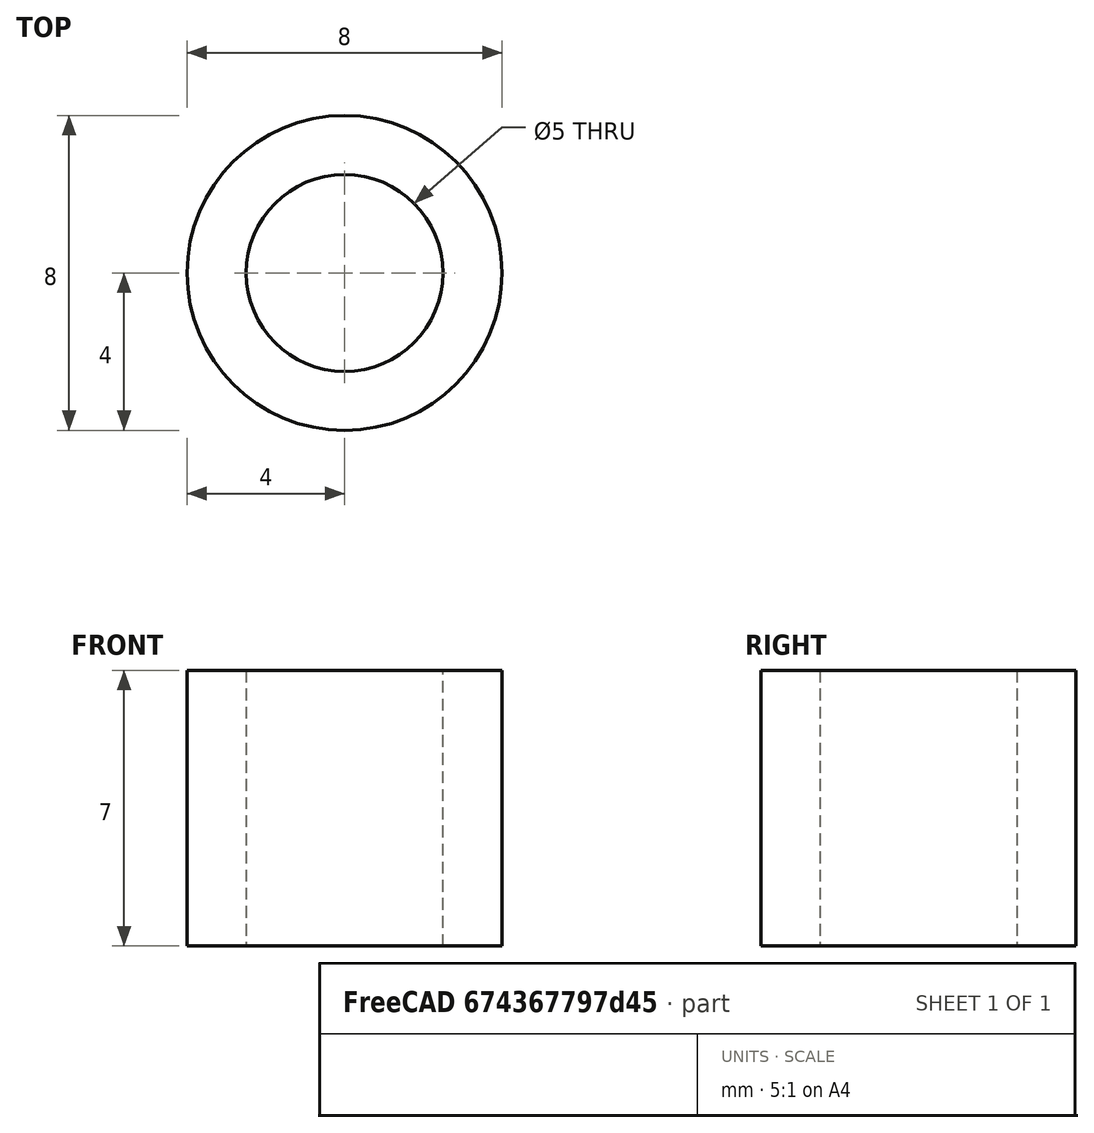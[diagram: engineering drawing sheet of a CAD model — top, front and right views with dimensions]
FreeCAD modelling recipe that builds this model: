
FCSTD DOCUMENT  (FreeCAD 0.19R24276 (Git))
Label: Vtulka_8x5x7
License: All rights reserved
LicenseURL: http://en.wikipedia.org/wiki/All_rights_reserved
objects: Sketcher::SketchObject×1, PartDesign::Pad×1, PartDesign::Body×1
note: 4 computed .brp shape members not serialized (recipe doc carries the construction recipe); baked Part::Feature solids carry a one-line shape summary decoded from their .brp

FEATURE [Sketcher::SketchObject] Sketch
  FullyConstrained = true
  MapMode = 5
  Support = -> [XY_Plane]
  sketch-geometry (2):
    g0: Circle CenterX=0 CenterY=0 CenterZ=0 NormalX=0 NormalY=0 NormalZ=1 AngleXU=0 Radius=2.5
    g1: Circle CenterX=0 CenterY=0 CenterZ=0 NormalX=0 NormalY=0 NormalZ=1 AngleXU=0 Radius=4
  constraints (4):
    c: Coincident(g0,g-1)
    c: Coincident(g1,g0)
    c: Diameter(g0) = 5
    c: Diameter(g1) = 8
FEATURE [PartDesign::Pad] Pad
  Direction = (1,1,1)
  Length = 7
  Length2 = 100
  Profile = -> Sketch
  Type = 0
FEATURE [PartDesign::Body] Body
  Group = -> [Sketch,Pad]
  Origin = -> Origin
  Tip = -> Pad
